FCSTD DOCUMENT  (FreeCAD 1.1R20260106 (Git shallow))
Label: top-assembly
License: All rights reserved
LicenseURL: https://en.wikipedia.org/wiki/All_rights_reserved
objects: App::Link×15, App::Point×3, Assembly::AssemblyLink×2, Assembly::JointGroup×1, Assembly::AssemblyObject×1
EXTERNAL_REF file=extruder-assembly.FCStd obj=Assembly
EXTERNAL_REF file=extruder-assembly.FCStd obj=Body
EXTERNAL_REF file=extruder-assembly.FCStd obj=Nema_11
EXTERNAL_REF file=extruder-assembly.FCStd obj=Body001
EXTERNAL_REF file=extruder-assembly.FCStd obj=Screw
EXTERNAL_REF file=extruder-assembly.FCStd obj=Screw001
EXTERNAL_REF file=extruder-assembly.FCStd obj=Screw002
EXTERNAL_REF file=extruder-assembly.FCStd obj=Screw003
EXTERNAL_REF file=extruder-assembly.FCStd obj=Nut
EXTERNAL_REF file=extruder-assembly.FCStd obj=Body002
EXTERNAL_REF file=extruder-assembly.FCStd obj=Screw004
EXTERNAL_REF file=cartridge-assembly.FCStd obj=Assembly
EXTERNAL_REF file=cartridge-assembly.FCStd obj=Body
EXTERNAL_REF file=cartridge-assembly.FCStd obj=Body002
EXTERNAL_REF file=cartridge-assembly.FCStd obj=Nut
EXTERNAL_REF file=cartridge-assembly.FCStd obj=ThreadedRod
EXTERNAL_REF file=cartridge-assembly.FCStd obj=Body003

FEATURE [App::Point] Origin001
  Role = Origin
FEATURE [Assembly::JointGroup] Joints
FEATURE [App::Point] Origin003
  Role = Origin
FEATURE [App::Link] Body
  LinkPlacement = pos=(2.73483,-1.24267,0) rot=(0,0,-1;0.109956rad)
  LinkedObject = -> <external extruder-assembly.FCStd>#Body
  Placement = pos=(2.73483,-1.24267,0) rot=(0,0,-1;0.109956rad)
FEATURE [App::Link] Nema_11  label="Nema-11"
  LinkPlacement = pos=(-4.75,-15.75,20) rot=(-0.707107,0.707107,0;3.14159rad)
  LinkedObject = -> <external extruder-assembly.FCStd>#Nema_11
  Placement = pos=(-4.75,-15.75,20) rot=(-0.707107,0.707107,0;3.14159rad)
FEATURE [App::Link] Body001
  LinkPlacement = pos=(-4.74999,-15.8,30.2) rot=(0,0,1;0rad)
  LinkedObject = -> <external extruder-assembly.FCStd>#Body001
  Placement = pos=(-4.74999,-15.8,30.2) rot=(0,0,1;0rad)
FEATURE [App::Link] Screw  label="M2.5x5-Screw"
  LinkPlacement = pos=(6.75,-4.25,22.55) rot=(0,0,1;0rad)
  LinkedObject = -> <external extruder-assembly.FCStd>#Screw
  Placement = pos=(6.75,-4.25,22.55) rot=(0,0,1;0rad)
FEATURE [App::Link] Screw001  label="M2.5x5-Screw002"
  LinkPlacement = pos=(6.75,-27.25,22.55) rot=(0,0,1;0rad)
  LinkedObject = -> <external extruder-assembly.FCStd>#Screw001
  Placement = pos=(6.75,-27.25,22.55) rot=(0,0,1;0rad)
FEATURE [App::Link] Screw002  label="M2.5x5-Screw004"
  LinkPlacement = pos=(-16.25,-27.2,22.55) rot=(0,0,1;0rad)
  LinkedObject = -> <external extruder-assembly.FCStd>#Screw002
  Placement = pos=(-16.25,-27.2,22.55) rot=(0,0,1;0rad)
FEATURE [App::Link] Screw003  label="M2.5x5-Screw006"
  LinkPlacement = pos=(-16.25,-4.25,22.55) rot=(0,0,1;0rad)
  LinkedObject = -> <external extruder-assembly.FCStd>#Screw003
  Placement = pos=(-16.25,-4.25,22.55) rot=(0,0,1;0rad)
FEATURE [App::Link] Nut  label="M3-Nut"
  LinkPlacement = pos=(15.15,-25.75,10) rot=(0,1,0;1.5708rad)
  LinkedObject = -> <external extruder-assembly.FCStd>#Nut
  Placement = pos=(15.15,-25.75,10) rot=(0,1,0;1.5708rad)
FEATURE [App::Link] Body002
  LinkPlacement = pos=(26.2,-0.749811,22.3498) rot=(-1,0,0;1.5708rad)
  LinkedObject = -> <external extruder-assembly.FCStd>#Body002
  Placement = pos=(26.2,-0.749811,22.3498) rot=(-1,0,0;1.5708rad)
FEATURE [App::Link] Screw004  label="M3x20-Screw"
  LinkPlacement = pos=(32.7,-25.75,10) rot=(0,1,0;1.5708rad)
  LinkedObject = -> <external extruder-assembly.FCStd>#Screw004
  Placement = pos=(32.7,-25.75,10) rot=(0,1,0;1.5708rad)
FEATURE [Assembly::AssemblyLink] Assembly001  label="Assembly"
  Group = -> [Body,Nema_11,Body001,Screw,Screw001,Screw002,Screw003,Nut,Body002,Screw004]
  LinkedObject = -> <external extruder-assembly.FCStd>#Assembly
  Origin = -> Origin002
  Placement = pos=(4e-16,0,0) rot=(0,0,1;0rad)
  Rigid = true
FEATURE [App::Point] Origin005  label="Origin006"
  Role = Origin
FEATURE [App::Link] Body003
  LinkedObject = -> <external cartridge-assembly.FCStd>#Body
FEATURE [App::Link] Body004
  LinkPlacement = pos=(0.0737821,0.0237821,5.17378) rot=(0,0,1;0rad)
  LinkedObject = -> <external cartridge-assembly.FCStd>#Body002
  Placement = pos=(0.0737821,0.0237821,5.17378) rot=(0,0,1;0rad)
FEATURE [App::Link] Nut001  label="M3-Nut001"
  LinkPlacement = pos=(0.05,0.05,5.7) rot=(0,0,1;0rad)
  LinkedObject = -> <external cartridge-assembly.FCStd>#Nut
  Placement = pos=(0.05,0.05,5.7) rot=(0,0,1;0rad)
FEATURE [App::Link] ThreadedRod  label="M3x70-ThreadedRod"
  LinkPlacement = pos=(-1.45519e-11,-2.5034e-06,21) rot=(0,0,1;0rad)
  LinkedObject = -> <external cartridge-assembly.FCStd>#ThreadedRod
  Placement = pos=(-1.45519e-11,-2.5034e-06,21) rot=(0,0,1;0rad)
FEATURE [App::Link] Body005
  LinkPlacement = pos=(-1.19209e-07,0.000680947,-51.8988) rot=(-1,0,0;1.5708rad)
  LinkedObject = -> <external cartridge-assembly.FCStd>#Body003
  Placement = pos=(-1.19209e-07,0.000680947,-51.8988) rot=(-1,0,0;1.5708rad)
FEATURE [Assembly::AssemblyLink] Assembly002  label="Assembly"
  Group = -> [Body003,Body004,Nut001,ThreadedRod,Body005]
  LinkedObject = -> <external cartridge-assembly.FCStd>#Assembly
  Origin = -> Origin004
  Placement = pos=(21.023,-15.6801,25) rot=(0,0,-1;1.5708rad)
  Rigid = true
FEATURE [Assembly::AssemblyObject] Assembly
  Group = -> [Joints,Assembly001,Assembly002]
  Origin = -> Origin
  Type = Assembly

RESOLVED EXTERNAL PARTS (link-assembly join: the EXTERNAL_REF files above that resolve inside this repo's crawl, each included once):
---- part cartridge-assembly.FCStd = doc fcstd_7792a91f9d31 ----
FCSTD DOCUMENT  (FreeCAD 1.1R20260106 (Git shallow))
Label: cartridge-assembly
License: All rights reserved
LicenseURL: https://en.wikipedia.org/wiki/All_rights_reserved
objects: App::Link×3, Part::FeaturePython×2, App::Point×1, Assembly::JointGroup×1, Assembly::AssemblyObject×1
note: 2 computed .brp shape members not serialized (recipe doc carries the construction recipe); baked Part::Feature solids carry a one-line shape summary decoded from their .brp
EXTERNAL_REF file=OTS/luer.FCStd obj=Body
EXTERNAL_REF file=FDM/cartridge-gear.FCStd obj=Body001
EXTERNAL_REF file=FDM/plunger.FCStd obj=Body

FEATURE [App::Point] Origin001
  Role = Origin
FEATURE [Assembly::JointGroup] Joints
FEATURE [App::Link] Body
  LinkedObject = -> <external OTS/luer.FCStd>#Body
FEATURE [App::Link] Body002
  LinkPlacement = pos=(0.0737821,0.0237821,5.17378) rot=(0,0,1;0rad)
  LinkedObject = -> <external FDM/cartridge-gear.FCStd>#Body001
  Placement = pos=(0.0737821,0.0237821,5.17378) rot=(0,0,1;0rad)
FEATURE [Part::FeaturePython] Nut  label="M3-Nut"  # WARN: FeaturePython — macro-defined, semantics opaque (R4)
  Diameter = 4
  Invert = false
  LeftHanded = false
  MatchOuter = false
  OffsetAngle = 0
  Placement = pos=(0.05,0.05,5.7) rot=(0,0,1;0rad)
  Thread = false
  Type = 31
FEATURE [Part::FeaturePython] ThreadedRod  label="M3x70-ThreadedRod"  # WARN: FeaturePython — macro-defined, semantics opaque (R4)
  Diameter = 4
  DiameterCustom = 6
  Invert = false
  LeftHanded = false
  Length = 70
  MatchOuter = false
  OffsetAngle = 0
  PitchCustom = 1
  Placement = pos=(-1.45519e-11,-2.5034e-06,21) rot=(0,0,1;0rad)
  Thread = true
  Type = 4
FEATURE [App::Link] Body003
  LinkPlacement = pos=(-1.19209e-07,0.000680947,-51.8988) rot=(-1,0,0;1.5708rad)
  LinkedObject = -> <external FDM/plunger.FCStd>#Body
  Placement = pos=(-1.19209e-07,0.000680947,-51.8988) rot=(-1,0,0;1.5708rad)
FEATURE [Assembly::AssemblyObject] Assembly
  Group = -> [Joints,Body,Body002,Nut,ThreadedRod,Body003]
  Origin = -> Origin
  Type = Assembly
---- part extruder-assembly.FCStd = doc fcstd_91b1a1d63410 ----
FCSTD DOCUMENT  (FreeCAD 1.1R20260106 (Git shallow))
Label: extruder-assembly
License: All rights reserved
LicenseURL: https://en.wikipedia.org/wiki/All_rights_reserved
objects: Part::FeaturePython×6, App::Link×4, App::Point×1, Assembly::JointGroup×1, Assembly::AssemblyObject×1
note: 6 computed .brp shape members not serialized (recipe doc carries the construction recipe); baked Part::Feature solids carry a one-line shape summary decoded from their .brp
EXTERNAL_REF file=FDM/extruder-base.FCStd obj=Part__Mirroring
EXTERNAL_REF file=OTS/nema11.FCStd obj=Part__Feature
EXTERNAL_REF file=FDM/extruder-gear.FCStd obj=Body001
EXTERNAL_REF file=FDM/cartridge-clamp.FCStd obj=Part__Mirroring

FEATURE [App::Point] Origin001
  Role = Origin
FEATURE [Assembly::JointGroup] Joints
FEATURE [App::Link] Body
  LinkPlacement = pos=(2.73483,-1.24267,0) rot=(0,0,-1;0.109956rad)
  LinkedObject = -> <external FDM/extruder-base.FCStd>#Part__Mirroring
  Placement = pos=(2.73483,-1.24267,0) rot=(0,0,-1;0.109956rad)
FEATURE [App::Link] Nema_11  label="Nema-11"
  LinkPlacement = pos=(-4.75,-15.75,20) rot=(-0.707107,0.707107,0;3.14159rad)
  LinkedObject = -> <external OTS/nema11.FCStd>#Part__Feature
  Placement = pos=(-4.75,-15.75,20) rot=(-0.707107,0.707107,0;3.14159rad)
FEATURE [Part::FeaturePython] Screw  label="M2.5x5-Screw"  # WARN: FeaturePython — macro-defined, semantics opaque (R4)
  Diameter = 3
  Invert = false
  LeftHanded = false
  Length = 10
  LengthCustom = 5
  MatchOuter = false
  OffsetAngle = 0
  Placement = pos=(6.75,-4.25,22.55) rot=(0,0,1;0rad)
  Thread = false
  Type = 75
FEATURE [Part::FeaturePython] Screw001  label="M2.5x5-Screw002"  # WARN: FeaturePython — macro-defined, semantics opaque (R4)
  Diameter = 3
  Invert = false
  LeftHanded = false
  Length = 10
  LengthCustom = 5
  MatchOuter = false
  OffsetAngle = 0
  Placement = pos=(6.75,-27.25,22.55) rot=(0,0,1;0rad)
  Thread = false
  Type = 75
FEATURE [Part::FeaturePython] Screw002  label="M2.5x5-Screw004"  # WARN: FeaturePython — macro-defined, semantics opaque (R4)
  Diameter = 3
  Invert = false
  LeftHanded = false
  Length = 10
  LengthCustom = 5
  MatchOuter = false
  OffsetAngle = 0
  Placement = pos=(-16.25,-27.2,22.55) rot=(0,0,1;0rad)
  Thread = false
  Type = 75
FEATURE [Part::FeaturePython] Screw003  label="M2.5x5-Screw006"  # WARN: FeaturePython — macro-defined, semantics opaque (R4)
  Diameter = 3
  Invert = false
  LeftHanded = false
  Length = 10
  LengthCustom = 5
  MatchOuter = false
  OffsetAngle = 0
  Placement = pos=(-16.25,-4.25,22.55) rot=(0,0,1;0rad)
  Thread = false
  Type = 75
FEATURE [Part::FeaturePython] Nut  label="M3-Nut"  # WARN: FeaturePython — macro-defined, semantics opaque (R4)
  Diameter = 4
  Invert = false
  LeftHanded = false
  MatchOuter = false
  OffsetAngle = 0
  Placement = pos=(15.15,-25.75,10) rot=(0,1,0;1.5708rad)
  Thread = false
  Type = 12
FEATURE [App::Link] Body001
  LinkPlacement = pos=(-4.74999,-15.8,30.2) rot=(0,0,1;0rad)
  LinkedObject = -> <external FDM/extruder-gear.FCStd>#Body001
  Placement = pos=(-4.74999,-15.8,30.2) rot=(0,0,1;0rad)
FEATURE [App::Link] Body002
  LinkPlacement = pos=(26.2,-0.749811,22.3498) rot=(-1,0,0;1.5708rad)
  LinkedObject = -> <external FDM/cartridge-clamp.FCStd>#Part__Mirroring
  Placement = pos=(26.2,-0.749811,22.3498) rot=(-1,0,0;1.5708rad)
FEATURE [Part::FeaturePython] Screw004  label="M3x20-Screw"  # WARN: FeaturePython — macro-defined, semantics opaque (R4)
  Diameter = 4
  Invert = false
  LeftHanded = false
  Length = 7
  LengthCustom = 20
  MatchOuter = false
  OffsetAngle = 0
  Placement = pos=(32.7,-25.75,10) rot=(0,1,0;1.5708rad)
  Thread = false
  Type = 75
FEATURE [Assembly::AssemblyObject] Assembly
  Group = -> [Joints,Body,Nema_11,Body001,Screw,Screw001,Screw002,Screw003,Nut,Body002,Screw004]
  Origin = -> Origin
  Type = Assembly
